# Revit family: Graypants_Scraplights_Classics_Disc_16_20_24_28_32_Pendant_R21_0925
name_source: partatom
category: Lighting Fixtures
units: mm (PartAtom-declared; Revit-internal decimal feet)

## family parameters
Cut with Voids When Loaded = No
Host = Face
Light Source = Yes
Part Type = Normal
Room Calculation Point = No
Round Connector Dimension = Use Diameter
Shared = No

## types (5) — shared parameters
Color Filter = 16777215
Default Elevation = 4' - 0"
Dimming Lamp Color Temperature Shift = <None>
Graypants_Cord/Canopy_Finish_Options = White | Black
Graypants_Manufacturer = Graypants
Graypants_Shade_Finish_Options = Natural Cardboard | Blonde Cardboard | White Cardboard
Graypants_URL = www.graypants.com
Light Source Symbol Size = 2' - 0"

## per-type parameters (varying)
| type | Graypants_Disc16_Canopy_Visible | Graypants_Disc16_Cord_Visible | Graypants_Disc16_Shade_Visible | Graypants_Disc20_Canopy_Visible | Graypants_Disc20_Cord_Visible | Graypants_Disc20_Shade_Visible | Graypants_Disc24_Canopy_Visible | Graypants_Disc24_Cord_Visible | Graypants_Disc24_Shade_Visible | Graypants_Disc28_Canopy_Visible | Graypants_Disc28_Cord_Visible | Graypants_Disc28_Shade_Visible | Graypants_Disc32_Canopy_Visible | Graypants_Disc32_Cord_Visible | Graypants_Disc32_Shade_Visible | Graypants_Model |
| Graypants_Scraplights_Disc16_Pendant | Yes | Yes | Yes | No | No | No | No | No | No | No | No | No | No | No | No | Scraplights_Classics_Disc_16 |
| Graypants_Scraplights_Disc20_Pendant | No | No | No | Yes | Yes | Yes | No | No | No | No | No | No | No | No | No | Scraplights_Classics_Disc_20 |
| Graypants_Scraplights_Disc24_Pendant | No | No | No | No | No | No | Yes | Yes | Yes | No | No | No | No | No | No | Scraplights_Classics_Disc_24 |
| Graypants_Scraplights_Disc28_Pendant | No | No | No | No | No | No | No | No | No | Yes | Yes | Yes | No | No | No | Scraplights_Classics_Disc_28 |
| Graypants_Scraplights_Disc32_Pendant | No | No | No | No | No | No | No | No | No | No | No | No | Yes | Yes | Yes | Scraplights_Classics_Disc_32 |

## geometry (parser evidence)
native form markers: Sweep x16
no freeform markers — native parametric forms only
